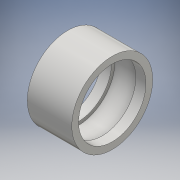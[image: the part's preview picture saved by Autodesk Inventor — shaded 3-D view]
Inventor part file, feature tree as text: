
AUTODESK INVENTOR PART (.ipt)
format: ipt  version: 2016 (Build 200138000, 138)  size: 148,480 bytes
history: native  units: mm
features: extrude x3, sketch x3
ambient origin geometry x8: Origin, YZ Plane, XZ Plane, XY Plane, X Axis, Y Axis, Z Axis, Center Point
bodies: Solid1 (feature_tree)
feature tree (6):
  extrude  "Extrusion1"  Depth=22.0mm
  extrude  "Extrusion3"  TaperAngle=0.0deg  [1 undecoded]
  extrude  "Extrusion4"  Depth=3.0mm
  sketch  "Sketch1"  dims[d0=24.0mm d1=22.0mm]
  sketch  "Sketch4"  dims[d2=13.2mm d3=0.0mm]
  sketch  "Sketch5"  dims[d9=20.0mm d10=22.0mm d11=3.0mm d12=0.0mm d13=20.0mm d14=22.0mm d15=3.0mm d16=0.0mm]
note: 1 required parameter value undecoded (feature->parameter linkage not recoverable at this tier; creation-order binding heuristic only, values carry confidence <= 0.55)
